# Revit family: CENTUM Zugstabanschluss M12
name_source: partatom
category: HLS-Bauteile
revit_build: Autodesk Revit 2017 (Build: 20190507_1515(x64)
units: mm (PartAtom-declared; Revit-internal decimal feet)

## family parameters
Arbeitsebenenbasiert = Ja
Beim Laden mit Abzugskörper schneiden = Nein
Bemaßung runder Anschluss = Durchmesser verwenden
Gemeinsam genutzt = Ja
Immer vertikal = Nein
Raumberechnungspunkt = Nein
Teiletyp = Normal

## types (2) — shared parameters
A = 20 mm  [stored 0.0656168 ft]
Bohrung = Bohrloch : Bohrloch 14
Fabrikat = MEFA
Firma = MEFA Befestigungs- und Montagesysteme GmbH
Kurztext1 = Zugstabanschluss M12
Material = Stahl
Mengeneinheit = St
Platte = MEFA Platte : Platte  60x 50x10
Vorgabe-Ansicht = 1219 mm
vpe = 1 St

## per-type parameters (varying)
| type | Artikelnummer | EAN | Gewicht | Gewicht pro Bauteil | Kurztext2 | Massivanschluss |
| CENTUM Zugstabanschluss M12 XL100/XL200 | 1621004010 | 4250928449610 | 2.07 kg | 2.07 kg | für Profiltyp XL 100, XL 200 | TL-XL Massivanschluss hängend : Massivanschluss XL100 hängend (9000597) |
| CENTUM Zugstabanschluss M12 XL120 | 1621204010 | 4250928449634 | 2.21 kg | 2.21 kg | für Profiltyp XL 120 | TL-XL Massivanschluss hängend : Massivanschluss XL120 hängend hoch (9000598) |

note: [stored X ft] marks values corroborated as IEEE doubles in the binary element streams (Revit-internal decimal feet)
